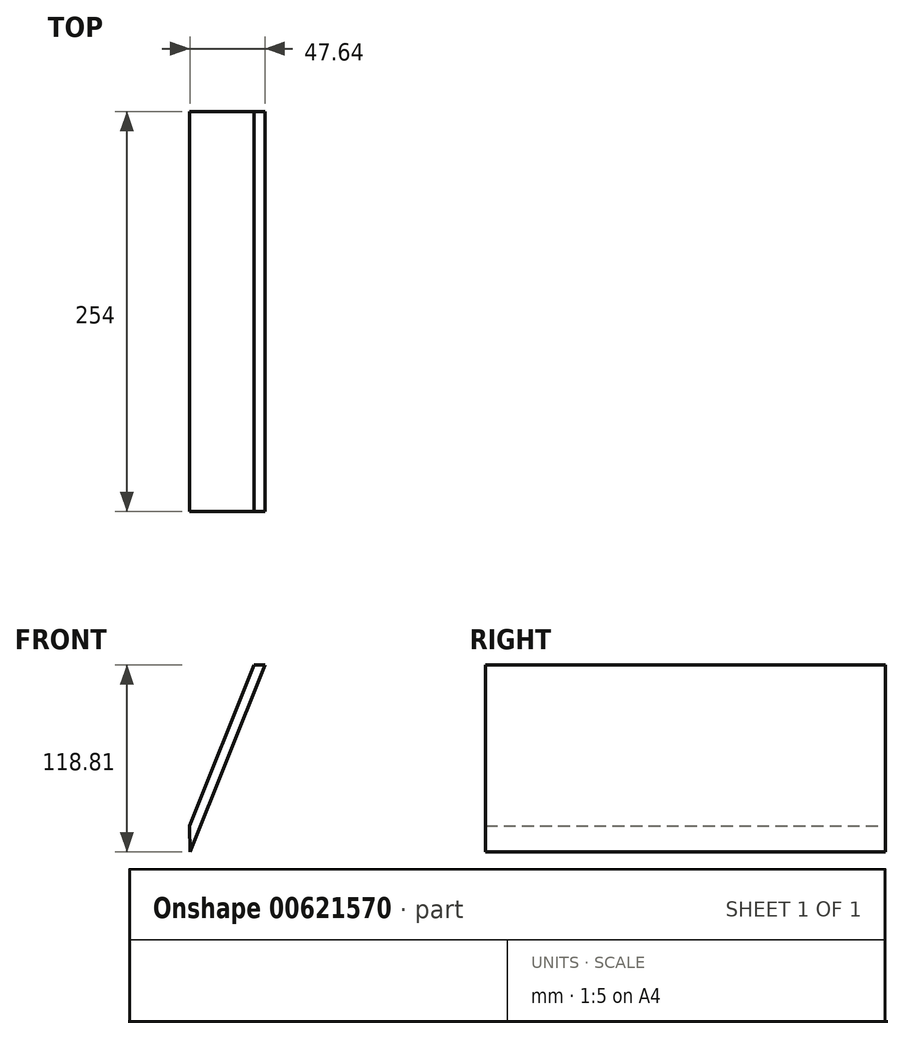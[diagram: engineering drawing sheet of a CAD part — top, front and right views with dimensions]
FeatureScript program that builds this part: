
annotation { "Feature Type Name" : "Feature", "Feature Type Description" : "" }
export const myFeature = defineFeature(function(context is Context, id is Id, definition is map)
    precondition{}
    {
        {
            var Q0;
            Q0=qCreatedBy(makeId("Front.planeOp"),FACE);
            var sketch = newSketch(context, id + "F0", { "sketchPlane" : qUnion([Q0])});
            skLineSegment(sketch, "E0", {"start": v(0, 0) * mm, "end": v(-40.77, -102.13) * mm});
            skLineSegment(sketch, "E1", {"start": v(0, 0) * mm, "end": v(29.4, 0.38) * mm});
            skLineSegment(sketch, "E2", {"start": v(-40.77, -102.13) * mm, "end": v(-40.06, -157.9) * mm});
            skLineSegment(sketch, "E3.0", {"start": v(6.87, 0.09) * mm, "end": v(-40.56, -118.72) * mm});
            skSolve(sketch);
        }
        {
            var Q0;
            Q0 = qSketchRegion(id + "F0", true);
            extrude(context, id + "F1", {"entities" : qUnion([Q0]), "depth" : 254 * mm, "offsetDistance" : 25.4 * mm});
        }
    });
